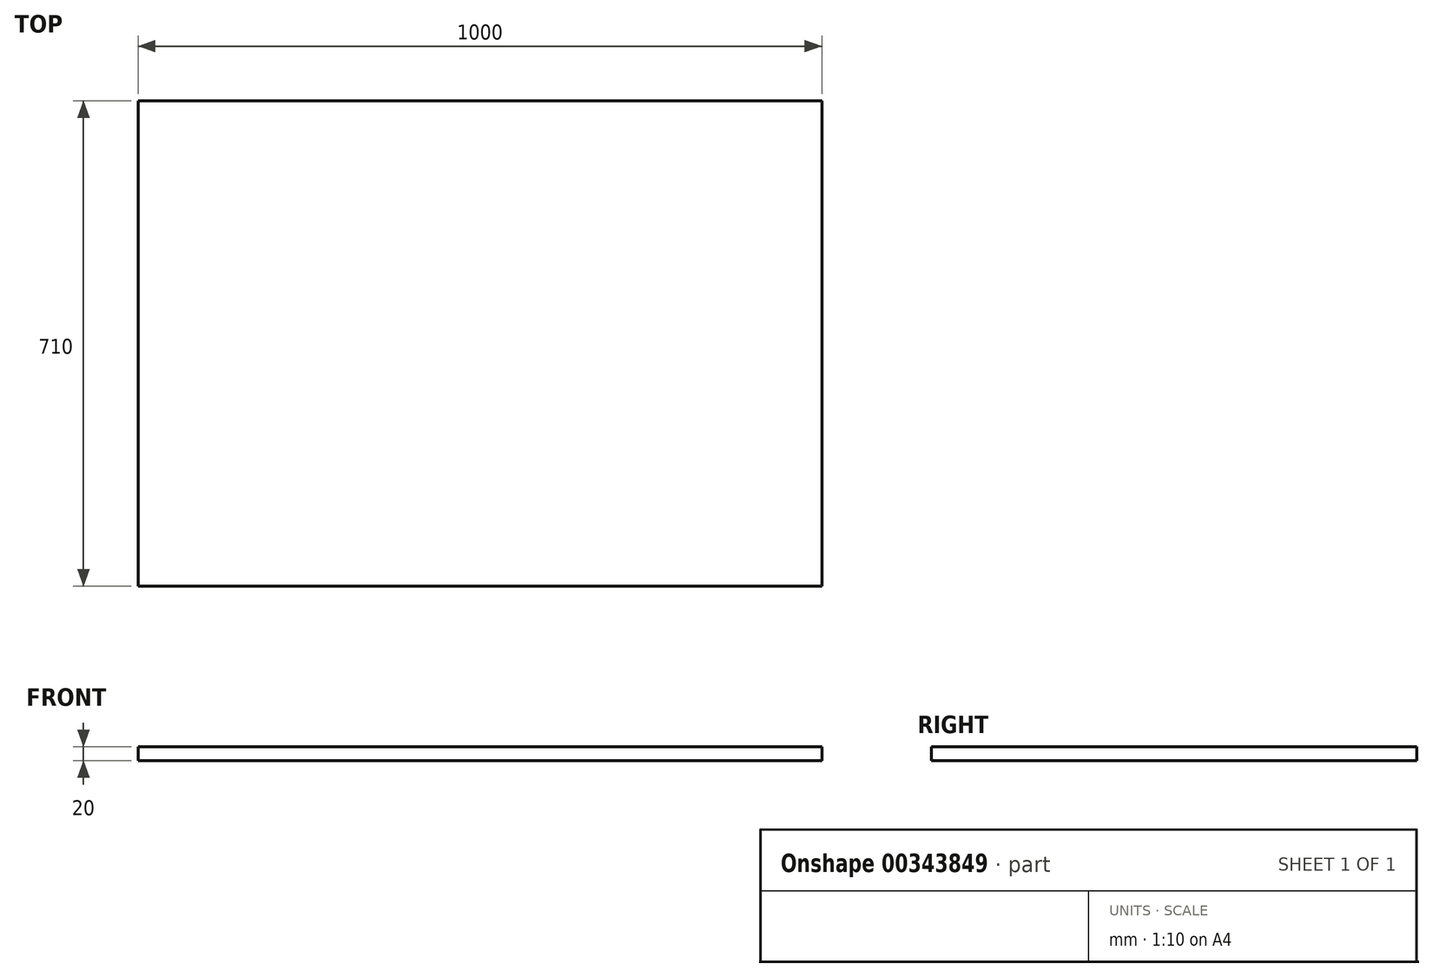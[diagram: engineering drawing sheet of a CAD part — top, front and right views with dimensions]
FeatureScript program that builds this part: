
annotation { "Feature Type Name" : "Feature", "Feature Type Description" : "" }
export const myFeature = defineFeature(function(context is Context, id is Id, definition is map)
    precondition{}
    {
        {
            var Q0;
            Q0=qCreatedBy(makeId("Top.planeOp"),FACE);
            var sketch = newSketch(context, id + "F0", { "sketchPlane" : qUnion([Q0])});
            skLineSegment(sketch, "E0.bottom", {"start": v(0, 0) * mm, "end": v(1000, 0) * mm});
            skLineSegment(sketch, "E0.top", {"start": v(0, -710) * mm, "end": v(1000, -710) * mm});
            skLineSegment(sketch, "E0.left", {"start": v(0, 0) * mm, "end": v(0, -710) * mm});
            skLineSegment(sketch, "E0.right", {"start": v(1000, 0) * mm, "end": v(1000, -710) * mm});
            skSolve(sketch);
        }
        {
            var Q0;
            Q0 = qSketchRegion(id + "F0", true);
            extrude(context, id + "F1", {"entities" : qUnion([Q0]), "depth" : 20 * mm});
        }
    });
